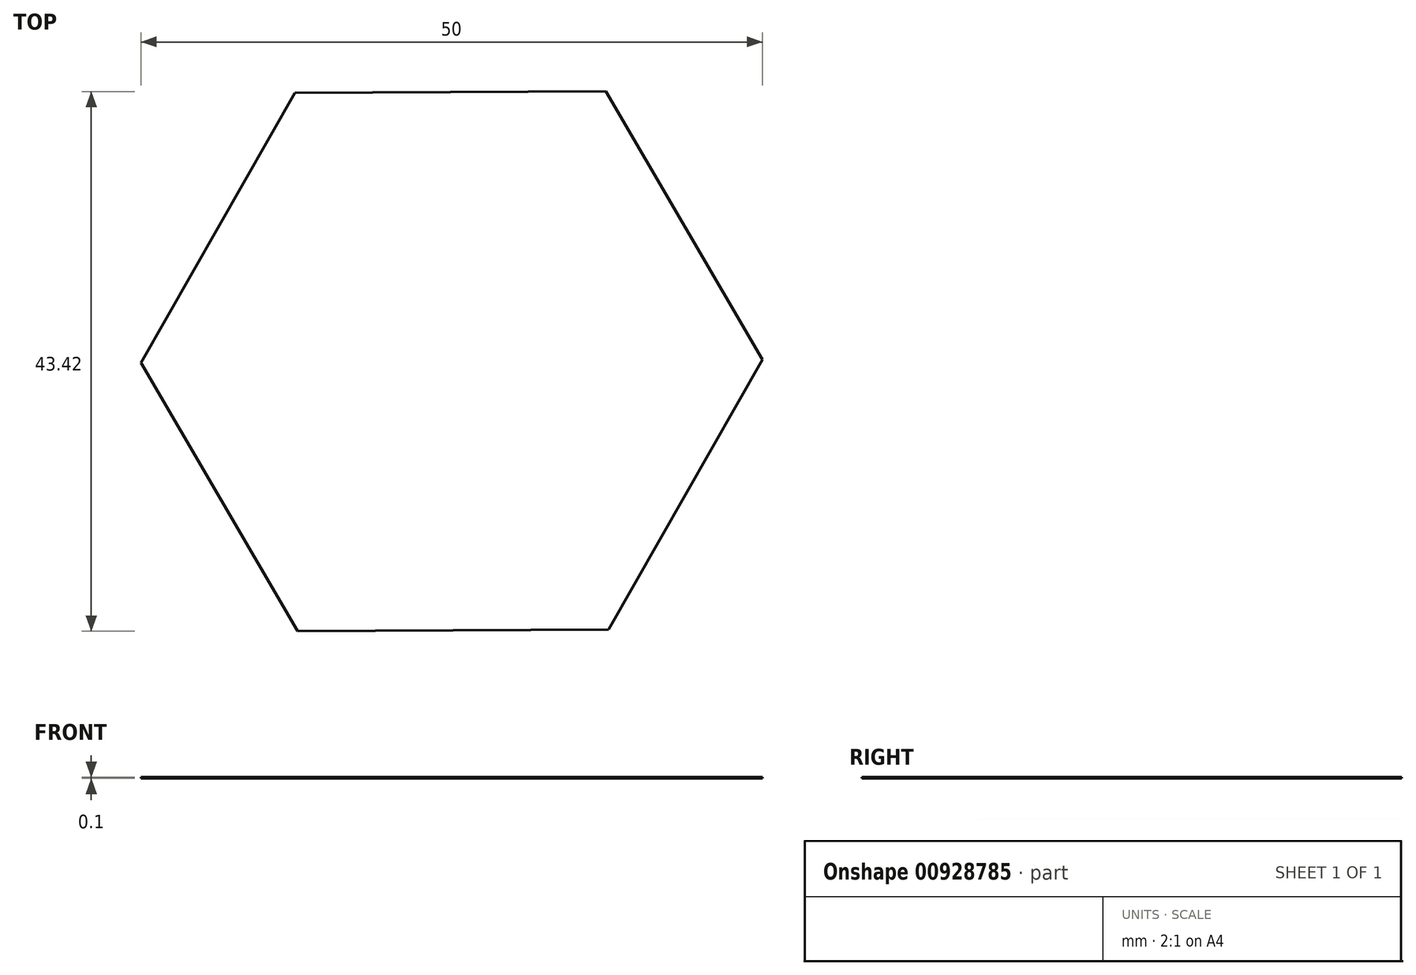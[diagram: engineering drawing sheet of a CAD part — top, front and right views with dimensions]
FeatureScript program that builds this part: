
annotation { "Feature Type Name" : "Feature", "Feature Type Description" : "" }
export const myFeature = defineFeature(function(context is Context, id is Id, definition is map)
    precondition{}
    {
        {
            var Q0;
            Q0=qCreatedBy(makeId("Top.planeOp"),FACE);
            var sketch = newSketch(context, id + "F0", { "sketchPlane" : qUnion([Q0])});
            skCircle(sketch, "E0.cCircle", {"center": v(0, 0) * mm, "radius": 21.65 * mm, "construction": true});
            skLineSegment(sketch, "E0.0", {"start": v(25, 0.13) * mm, "end": v(12.61, -21.59) * mm});
            skLineSegment(sketch, "E0.1", {"start": v(12.61, -21.59) * mm, "end": v(-12.39, -21.71) * mm});
            skLineSegment(sketch, "E0.2", {"start": v(-12.39, -21.71) * mm, "end": v(-25, -0.13) * mm});
            skLineSegment(sketch, "E0.3", {"start": v(-25, -0.13) * mm, "end": v(-12.61, 21.59) * mm});
            skLineSegment(sketch, "E0.4", {"start": v(-12.61, 21.59) * mm, "end": v(12.39, 21.71) * mm});
            skLineSegment(sketch, "E0.5", {"start": v(12.39, 21.71) * mm, "end": v(25, 0.13) * mm});
            skPoint(sketch, "E0.0.midPoint", {"position": v(18.8, -10.73) * mm});
            skSolve(sketch);
        }
        {
            var Q0;
            Q0=makeQuery(id+"F0.imprint","IMPRINT",FACE,{"disambiguationData":[TD([[makeQuery(id+"F0.imprint","IMPRINT",EDGE,{"derivedFrom":sQuery(id+"F0.wireOp",EDGE,"E0.0")}),-1.0]])]});
            extrude(context, id + "F1", {"entities" : qUnion([Q0]), "depth" : 0.1 * mm, "offsetDistance" : 25 * mm});
        }
    });
